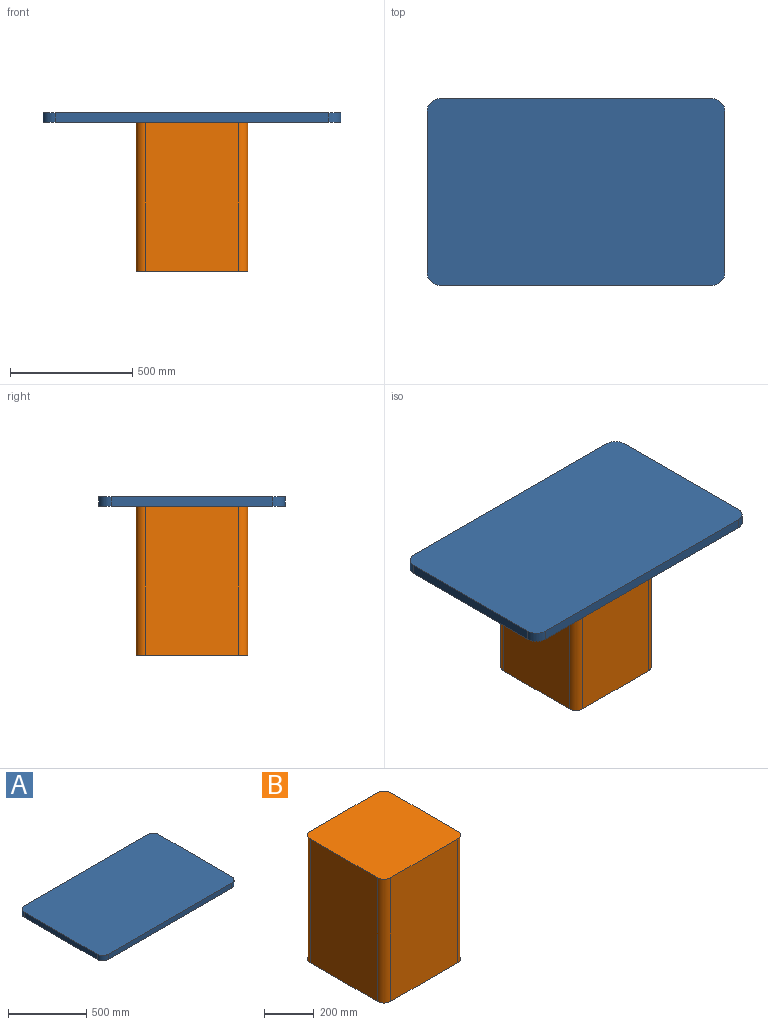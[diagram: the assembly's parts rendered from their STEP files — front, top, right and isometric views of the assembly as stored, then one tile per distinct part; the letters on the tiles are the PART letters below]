
ASSEMBLY  parts=2 mates=1
PART A: 10 faces, bbox 1219.2x762x40.6 mm
  f0: plane 660.4x40.64mm, normal (1,0,0), area 26838.7mm2, adj f4,f5,f6,f7
  f1: plane 1117.6x40.64mm, normal (0,1,0), area 45419.3mm2, adj f4,f5,f7,f8
  f2: plane 660.4x40.64mm, normal (-1,0,0), area 26838.7mm2, adj f4,f5,f8,f9
  f3: plane 1117.6x40.64mm, normal (0,-1,0), area 45419.3mm2, adj f4,f5,f6,f9
  f4: plane 1219.2x762mm, normal (0,0,1), area 926815.2mm2, adj f0,f1,f2,f3,f6,f7,f8,f9
  f5: plane 1219.2x762mm, normal (0,0,-1), area 926815.2mm2, adj f0,f1,f2,f3,f6,f7,f8,f9
  f6: cylinder r=50.8mm len=50.8mm, axis (0,0,1), area 3242.9mm2, adj f0,f3,f4,f5
  f7: cylinder r=50.8mm len=50.8mm, axis (0,0,-1), area 3242.9mm2, adj f0,f1,f4,f5
  f8: cylinder r=50.8mm len=50.8mm, axis (0,0,1), area 3242.9mm2, adj f1,f2,f4,f5
  f9: cylinder r=50.8mm len=50.8mm, axis (0,0,-1), area 3242.9mm2, adj f2,f3,f4,f5
PART B: 10 faces, bbox 457.2x457.2x609.6 mm
  f0: plane 609.6x381mm, normal (-1,0,0), area 232257.6mm2, adj f4,f5,f6,f9
  f1: plane 609.6x381mm, normal (0,-1,0), area 232257.6mm2, adj f4,f5,f6,f7
  f2: plane 609.6x381mm, normal (1,0,0), area 232257.6mm2, adj f4,f5,f7,f8
  f3: plane 609.6x381mm, normal (0,1,0), area 232257.6mm2, adj f4,f5,f8,f9
  f4: plane 457.2x457.2mm, normal (0,0,1), area 207785.8mm2, adj f0,f1,f2,f3,f6,f7,f8,f9
  f5: plane 457.2x457.2mm, normal (0,0,-1), area 207785.8mm2, adj f0,f1,f2,f3,f6,f7,f8,f9
  f6: cylinder r=38.1mm len=609.6mm, axis (0,0,1), area 36482.9mm2, adj f0,f1,f4,f5
  f7: cylinder r=38.1mm len=609.6mm, axis (0,0,-1), area 36482.9mm2, adj f1,f2,f4,f5
  f8: cylinder r=38.1mm len=609.6mm, axis (0,0,1), area 36482.9mm2, adj f2,f3,f4,f5
  f9: cylinder r=38.1mm len=609.6mm, axis (0,0,-1), area 36482.9mm2, adj f0,f3,f4,f5
PLACE A t=(856.01,-110.66,-25.4)mm
PLACE B at identity
MATE fastened A.f5 <-> B.f4  axis (0,0,-1) through (228.6,228.6,609.6)mm
